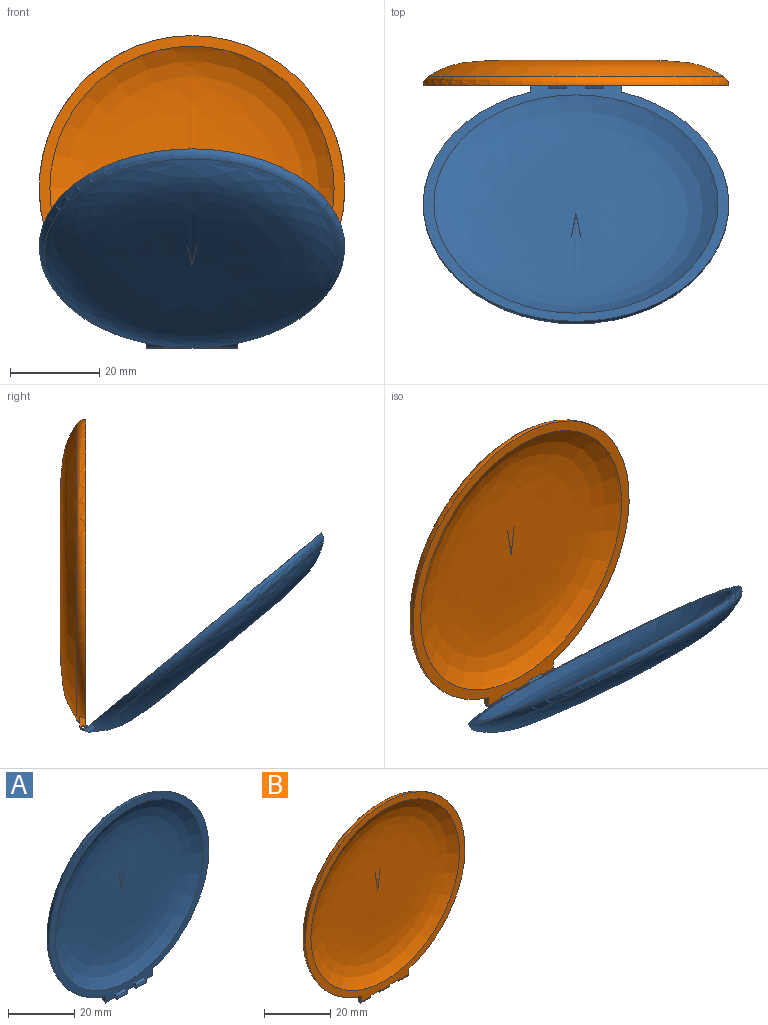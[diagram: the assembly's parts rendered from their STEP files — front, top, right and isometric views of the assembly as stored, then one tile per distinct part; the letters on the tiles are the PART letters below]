
ASSEMBLY  parts=2 mates=1
PART A: 21 faces, bbox 73.9x7.4x73.9 mm
  f0: plane 2.8x1.27mm, normal (1,0,0), area 2.7mm2, adj f5,f6,f8,f10,f20
  f1: plane 2.8x1.27mm, normal (-1,0,0), area 2.7mm2, adj f5,f6,f8,f10,f20
  f2: plane 4.06x0.95mm, normal (0,-0.5,0.87), area 4.4mm2, adj f4,f6,f14,f15
  f3: cylinder r=0.64mm len=4.06mm, axis (1,0,0), area 4mm2, adj f4,f5,f14,f15
  f4: cylinder r=0.64mm len=4.06mm, axis (1,0,0), area 4.1mm2, adj f2,f3,f14,f15
  f5: plane 20.32x1.33mm, normal (0,0.5,-0.87), area 26.8mm2, adj f0,f1,f3,f6,f12,f14,f15,f16
  f6: plane 69.14x68.28mm, normal (0,-1,0), area 510.3mm2, adj f0,f1,f2,f5,f8,f9,f11,f14
  f7: revolved ~66.04x66.04mm, area 3558.8mm2, adj f8
  f8: torus R=31.75mm, axis (0,-1,0), area 483.8mm2, adj f0,f1,f6,f7,f10
  f9: revolved ~63.5x63.5mm, area 3283.3mm2, adj f6
  f10: plane 20.32x1.77mm, normal (0,1,0), area 14.7mm2, adj f0,f1,f8,f20
  f11: plane 4.06x0.95mm, normal (0,-0.5,0.87), area 4.4mm2, adj f6,f13,f16,f17
  f12: cylinder r=0.64mm len=4.06mm, axis (1,0,0), area 4mm2, adj f5,f13,f16,f17
  f13: cylinder r=0.64mm len=4.06mm, axis (1,0,0), area 4.1mm2, adj f11,f12,f16,f17
  f14: plane 1.73x1.26mm, normal (1,0,0), area 1.2mm2, adj f2,f3,f4,f5,f6,f18
  f15: plane 1.73x1.26mm, normal (-1,0,0), area 1.2mm2, adj f2,f3,f4,f5,f6,f18
  f16: plane 1.73x1.26mm, normal (1,0,0), area 1.2mm2, adj f5,f6,f11,f12,f13,f19
  f17: plane 1.73x1.26mm, normal (-1,0,0), area 1.2mm2, adj f5,f6,f11,f12,f13,f19
  f18: cylinder r=0.32mm len=4.06mm, axis (1,0,0), area 8.1mm2, adj f14,f15
  f19: cylinder r=0.32mm len=4.06mm, axis (1,0,0), area 8.1mm2, adj f16,f17
  f20: cylinder r=0.51mm len=20.32mm, axis (1,0,0), area 10.8mm2, adj f0,f1,f5,f10
PART B: 19 faces, bbox 73.9x7.4x73.9 mm
  f0: plane 68.76x68.28mm, normal (0,-1,0), area 511.4mm2, adj f1,f2,f3,f4,f5,f6,f8,f10
  f1: plane 3.05x1.27mm, normal (1,0,0), area 3.1mm2, adj f0,f7,f8,f13,f14
  f2: plane 3.05x1.27mm, normal (-1,0,0), area 3.1mm2, adj f0,f7,f8,f17,f18
  f3: plane 1.27x1.01mm, normal (1,0,0), area 0.8mm2, adj f0,f7,f11,f17,f18
  f4: plane 1.27x1.01mm, normal (-1,0,0), area 0.8mm2, adj f0,f7,f11,f15,f16
  f5: plane 1.27x1.01mm, normal (1,0,0), area 0.8mm2, adj f0,f7,f12,f15,f16
  f6: plane 1.27x1.01mm, normal (-1,0,0), area 0.8mm2, adj f0,f7,f12,f13,f14
  f7: plane 20.32x2.42mm, normal (0,1,0), area 24.7mm2, adj f1,f2,f3,f4,f5,f6,f8,f11
  f8: torus R=31.75mm, axis (0,-1,0), area 484.8mm2, adj f0,f1,f2,f7,f9
  f9: revolved ~66.03x66.03mm, area 3556.9mm2, adj f8
  f10: revolved ~63.5x63.5mm, area 3282.6mm2, adj f0
  f11: plane 4.06x1.27mm, normal (0,0,-1), area 5.2mm2, adj f0,f3,f4,f7
  f12: plane 4.06x1.27mm, normal (0,0,-1), area 5.2mm2, adj f0,f5,f6,f7
  f13: cylinder r=0.32mm len=4.06mm, axis (1,0,0), area 8.1mm2, adj f1,f6
  f14: cylinder r=0.64mm len=4.06mm, axis (1,0,0), area 8.1mm2, adj f0,f1,f6,f7
  f15: cylinder r=0.32mm len=4.06mm, axis (1,0,0), area 8.1mm2, adj f4,f5
  f16: cylinder r=0.64mm len=4.06mm, axis (1,0,0), area 8.1mm2, adj f0,f4,f5,f7
  f17: cylinder r=0.32mm len=4.06mm, axis (1,0,0), area 8.1mm2, adj f2,f3
  f18: cylinder r=0.64mm len=4.06mm, axis (1,0,0), area 8.1mm2, adj f0,f2,f3,f7
PLACE A rot(axis=(0,0.43,-0.91),180deg) t=(1.4,-26.32,-9.15)mm
PLACE B t=(1.4,0.1,3.84)mm fixed
MATE revolute B.f13 <-> A.f18  axis (1,0,0) through (7.5,0.73,-30.78)mm
